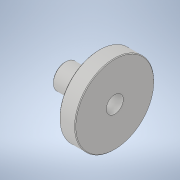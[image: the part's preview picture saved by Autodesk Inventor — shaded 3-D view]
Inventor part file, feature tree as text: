
AUTODESK INVENTOR PART (.ipt)
format: ipt  version: 2021 (Build 250183000, 183)  size: 119,808 bytes
history: native  units: in
note: dims shown in document units (in); Inventor stores cm internally (conversion verified against a paired STEP export)
features: extrude x2, sketch x2, chamfer x1
ambient origin geometry x8: Origin, YZ Plane, XZ Plane, XY Plane, X Axis, Y Axis, Z Axis, Center Point
bodies: Solid1 (feature_tree)
feature tree (5):
  extrude  "Extrusion1"  Depth=0.268in
  extrude  "Extrusion2"  Depth=0.25in
  chamfer  "Chamfer1"  Distance=0.25in
  sketch  "Sketch1"  dims[d0=0.394in d1=0.268in]
  sketch  "Sketch2"  dims[d2=0.532in d3=0.0in d4=1.25in d5=0.25in d6=0.0in d7=0.268in d9=0.01in d10=0.125in d11=45.0deg]
